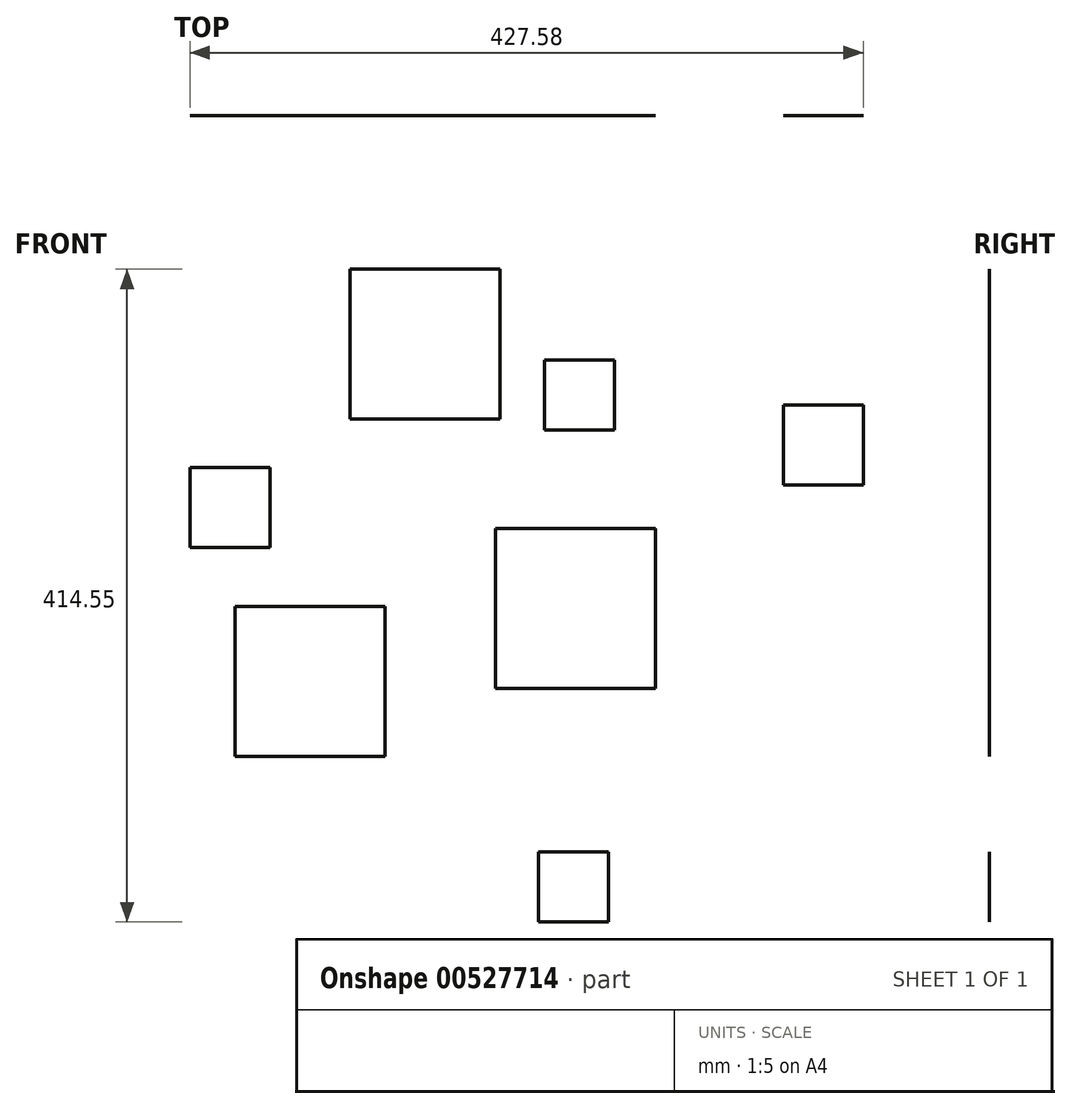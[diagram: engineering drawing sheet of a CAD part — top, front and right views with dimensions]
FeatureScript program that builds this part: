
annotation { "Feature Type Name" : "Feature", "Feature Type Description" : "" }
export const myFeature = defineFeature(function(context is Context, id is Id, definition is map)
    precondition{}
    {
        {
            var Q0;
            Q0=qCreatedBy(makeId("Front.planeOp"),FACE);
            var sketch = newSketch(context, id + "F0", { "sketchPlane" : qUnion([Q0])});
            skLineSegment(sketch, "E0.bottom", {"start": v(-75.53, -40.93) * mm, "end": v(26.07, -40.93) * mm});
            skLineSegment(sketch, "E0.top", {"start": v(-75.53, 60.67) * mm, "end": v(26.07, 60.67) * mm});
            skLineSegment(sketch, "E0.left", {"start": v(-75.53, -40.93) * mm, "end": v(-75.53, 60.67) * mm});
            skLineSegment(sketch, "E0.right", {"start": v(26.07, -40.93) * mm, "end": v(26.07, 60.67) * mm});
            skLineSegment(sketch, "E1.bottom", {"start": v(-240.95, -84.12) * mm, "end": v(-145.7, -84.12) * mm});
            skLineSegment(sketch, "E1.top", {"start": v(-240.95, 11.13) * mm, "end": v(-145.7, 11.13) * mm});
            skLineSegment(sketch, "E1.left", {"start": v(-240.95, -84.12) * mm, "end": v(-240.95, 11.13) * mm});
            skLineSegment(sketch, "E1.right", {"start": v(-145.7, -84.12) * mm, "end": v(-145.7, 11.13) * mm});
            skLineSegment(sketch, "E2.bottom", {"start": v(-269.54, 99.3) * mm, "end": v(-218.74, 99.3) * mm});
            skLineSegment(sketch, "E2.top", {"start": v(-269.54, 48.5) * mm, "end": v(-218.74, 48.5) * mm});
            skLineSegment(sketch, "E2.left", {"start": v(-269.54, 99.3) * mm, "end": v(-269.54, 48.5) * mm});
            skLineSegment(sketch, "E2.right", {"start": v(-218.74, 99.3) * mm, "end": v(-218.74, 48.5) * mm});
            skLineSegment(sketch, "E3.bottom", {"start": v(-44.45, 167.77) * mm, "end": v(0, 167.77) * mm});
            skLineSegment(sketch, "E3.top", {"start": v(-44.45, 123.32) * mm, "end": v(0, 123.32) * mm});
            skLineSegment(sketch, "E3.left", {"start": v(-44.45, 167.77) * mm, "end": v(-44.45, 123.32) * mm});
            skLineSegment(sketch, "E3.right", {"start": v(0, 167.77) * mm, "end": v(0, 123.32) * mm});
            skLineSegment(sketch, "E4.bottom", {"start": v(-168, 225.33) * mm, "end": v(-72.75, 225.33) * mm});
            skLineSegment(sketch, "E4.top", {"start": v(-168, 130.08) * mm, "end": v(-72.75, 130.08) * mm});
            skLineSegment(sketch, "E4.left", {"start": v(-168, 225.33) * mm, "end": v(-168, 130.08) * mm});
            skLineSegment(sketch, "E4.right", {"start": v(-72.75, 225.33) * mm, "end": v(-72.75, 130.08) * mm});
            skLineSegment(sketch, "E5.bottom", {"start": v(107.24, 139) * mm, "end": v(158.04, 139) * mm});
            skLineSegment(sketch, "E5.top", {"start": v(107.24, 88.2) * mm, "end": v(158.04, 88.2) * mm});
            skLineSegment(sketch, "E5.left", {"start": v(107.24, 139) * mm, "end": v(107.24, 88.2) * mm});
            skLineSegment(sketch, "E5.right", {"start": v(158.04, 139) * mm, "end": v(158.04, 88.2) * mm});
            skLineSegment(sketch, "E6.bottom", {"start": v(-48.2, -144.77) * mm, "end": v(-3.75, -144.77) * mm});
            skLineSegment(sketch, "E6.top", {"start": v(-48.2, -189.22) * mm, "end": v(-3.75, -189.22) * mm});
            skLineSegment(sketch, "E6.left", {"start": v(-48.2, -144.77) * mm, "end": v(-48.2, -189.22) * mm});
            skLineSegment(sketch, "E6.right", {"start": v(-3.75, -144.77) * mm, "end": v(-3.75, -189.22) * mm});
            skSolve(sketch);
        }
        {
            var Q0;
            Q0=makeQuery(id+"F0.imprint","IMPRINT",FACE,{"disambiguationData":[TD([[makeQuery(id+"F0.imprint","IMPRINT",EDGE,{"derivedFrom":sQuery(id+"F0.wireOp",EDGE,"E1.bottom")}),1.0]])]});
            var Q1;
            Q1=makeQuery(id+"F0.imprint","IMPRINT",FACE,{"disambiguationData":[TD([[makeQuery(id+"F0.imprint","IMPRINT",EDGE,{"derivedFrom":sQuery(id+"F0.wireOp",EDGE,"E2.bottom")}),-1.0]])]});
            var Q2;
            Q2=makeQuery(id+"F0.imprint","IMPRINT",FACE,{"disambiguationData":[TD([[makeQuery(id+"F0.imprint","IMPRINT",EDGE,{"derivedFrom":sQuery(id+"F0.wireOp",EDGE,"E0.bottom")}),1.0]])]});
            var Q3;
            Q3=makeQuery(id+"F0.imprint","IMPRINT",FACE,{"disambiguationData":[TD([[makeQuery(id+"F0.imprint","IMPRINT",EDGE,{"derivedFrom":sQuery(id+"F0.wireOp",EDGE,"E3.bottom")}),-1.0]])]});
            var Q4;
            Q4=makeQuery(id+"F0.imprint","IMPRINT",FACE,{"disambiguationData":[TD([[makeQuery(id+"F0.imprint","IMPRINT",EDGE,{"derivedFrom":sQuery(id+"F0.wireOp",EDGE,"E4.bottom")}),-1.0]])]});
            var Q5;
            Q5=makeQuery(id+"F0.imprint","IMPRINT",FACE,{"disambiguationData":[TD([[makeQuery(id+"F0.imprint","IMPRINT",EDGE,{"derivedFrom":sQuery(id+"F0.wireOp",EDGE,"E5.bottom")}),-1.0]])]});
            var Q6;
            Q6=makeQuery(id+"F0.imprint","IMPRINT",FACE,{"disambiguationData":[TD([[makeQuery(id+"F0.imprint","IMPRINT",EDGE,{"derivedFrom":sQuery(id+"F0.wireOp",EDGE,"E6.bottom")}),-1.0]])]});
            extrude(context, id + "F1", {"entities" : qUnion([Q0, Q1, Q2, Q3, Q4, Q5, Q6]), "depth" : 1 / 203.2 * mm, "offsetDistance" : 25.4 * mm});
        }
    });
